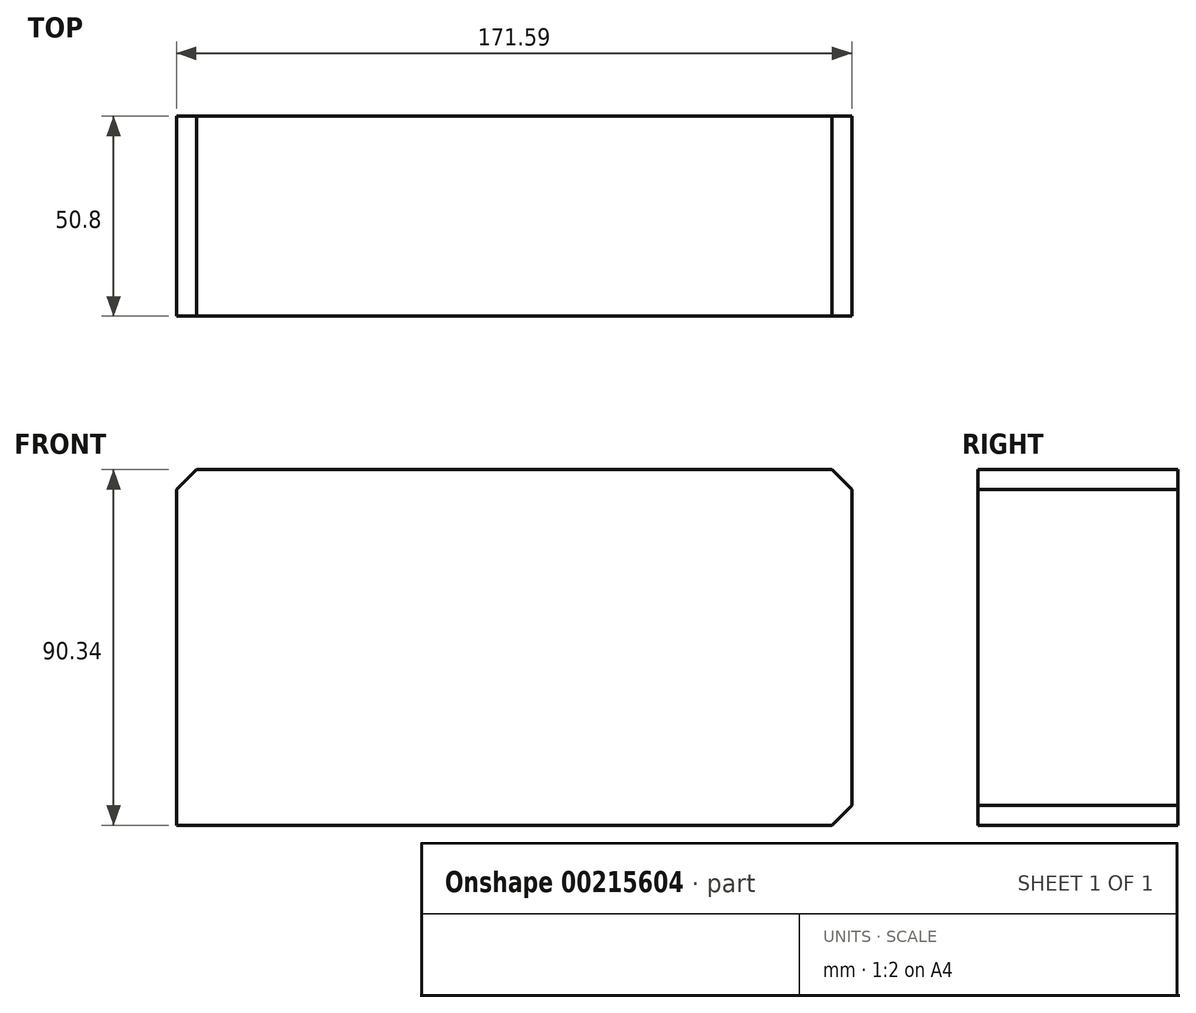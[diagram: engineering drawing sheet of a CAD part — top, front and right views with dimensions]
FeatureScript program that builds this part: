
annotation { "Feature Type Name" : "Feature", "Feature Type Description" : "" }
export const myFeature = defineFeature(function(context is Context, id is Id, definition is map)
    precondition{}
    {
        {
            var Q0;
            Q0=qCreatedBy(makeId("Front.planeOp"),FACE);
            var sketch = newSketch(context, id + "F0", { "sketchPlane" : qUnion([Q0])});
            skLineSegment(sketch, "E0.bottom", {"start": v(-76.24, 56.94) * mm, "end": v(95.35, 56.94) * mm});
            skLineSegment(sketch, "E0.top", {"start": v(-76.24, -33.4) * mm, "end": v(95.35, -33.4) * mm});
            skLineSegment(sketch, "E0.left", {"start": v(-76.24, 56.94) * mm, "end": v(-76.24, -33.4) * mm});
            skLineSegment(sketch, "E0.right", {"start": v(95.35, 56.94) * mm, "end": v(95.35, -33.4) * mm});
            skSolve(sketch);
        }
        {
            var Q0;
            Q0=makeQuery(id+"F0.imprint","IMPRINT",FACE,{"disambiguationData":[TD([[makeQuery(id+"F0.imprint","IMPRINT",EDGE,{"derivedFrom":sQuery(id+"F0.wireOp",EDGE,"E0.bottom")}),-1.0]])]});
            var Q1;
            Q1 = qSketchRegion(id + "F2", true);
            extrude(context, id + "F1", {"entities" : qUnion([Q0, Q1]), "depth" : 50.8 * mm});
        }
        {
            var Q0;
            Q0=makeQuery(id+"F1.opExtrude","CAP_FACE",FACE,{"disambiguationData":[OSD([sQuery(id+"F0.wireOp",EDGE,"E0.bottom"),sQuery(id+"F0.wireOp",EDGE,"E0.top"),sQuery(id+"F0.wireOp",EDGE,"E0.left"),sQuery(id+"F0.wireOp",EDGE,"E0.right")])],"isStart":false});
            var sketch = newSketch(context, id + "F2", { "sketchPlane" : qUnion([Q0])});
            skPoint(sketch, "E1", {"position": v(-29.14, 18.8) * mm});
            skLineSegment(sketch, "E2.bottom", {"start": v(0, 36.82) * mm, "end": v(43.28, 36.82) * mm});
            skLineSegment(sketch, "E2.top", {"start": v(0, 22.1) * mm, "end": v(43.28, 22.1) * mm});
            skLineSegment(sketch, "E2.left", {"start": v(0, 36.82) * mm, "end": v(0, 22.1) * mm});
            skLineSegment(sketch, "E2.right", {"start": v(43.28, 36.82) * mm, "end": v(43.28, 22.1) * mm});
            skSolve(sketch);
        }
        {
            var Q0;
            Q0=makeQuery(id+"F1.opExtrude","SWEPT_EDGE",EDGE,{"disambiguationData":[OSD([sQuery(id+"F0.wireOp",EDGE,"E0.bottom"),sQuery(id+"F0.wireOp",EDGE,"E0.left")])]});
            var Q1;
            Q1=makeQuery(id+"F1.opExtrude","SWEPT_EDGE",EDGE,{"disambiguationData":[OSD([sQuery(id+"F0.wireOp",EDGE,"E0.bottom"),sQuery(id+"F0.wireOp",EDGE,"E0.right")])]});
            var Q2;
            Q2=makeQuery(id+"F1.opExtrude","SWEPT_EDGE",EDGE,{"disambiguationData":[OSD([sQuery(id+"F0.wireOp",EDGE,"E0.top"),sQuery(id+"F0.wireOp",EDGE,"E0.right")])]});
            chamfer(context, id + "F3", {"entities" : qUnion([Q0, Q1, Q2]), "width" : 5.08 * mm, "tangentPropagation" : true});
        }
    });
